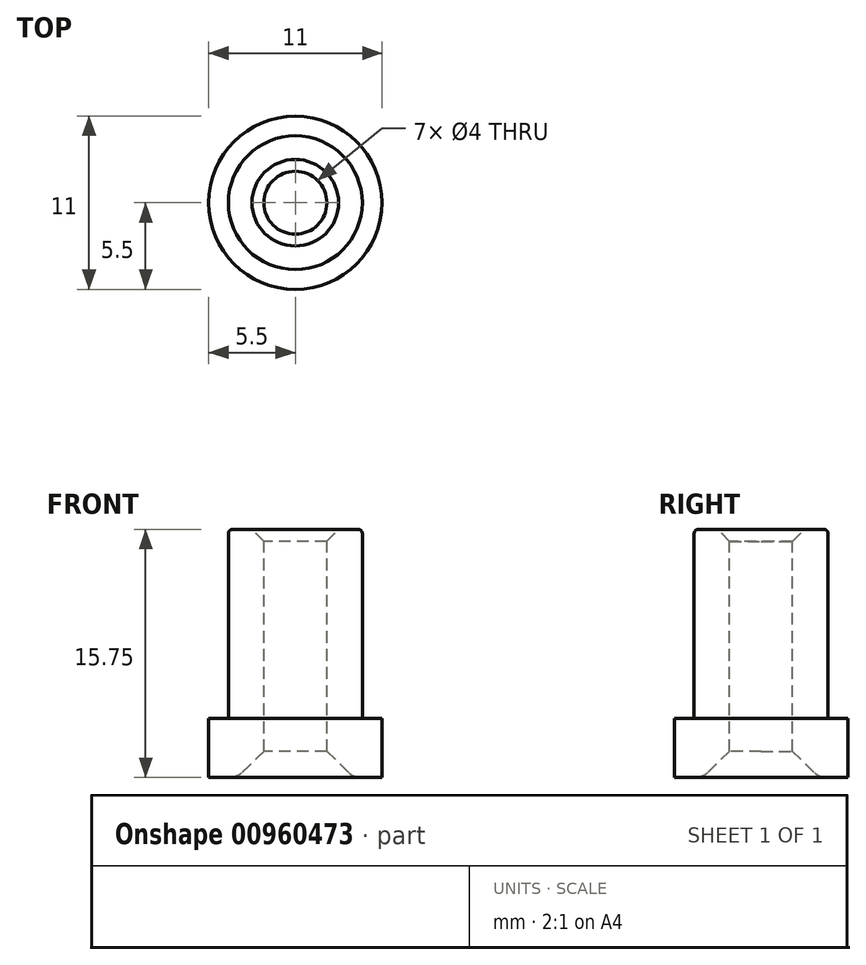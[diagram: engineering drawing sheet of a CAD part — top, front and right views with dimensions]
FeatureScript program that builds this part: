
annotation { "Feature Type Name" : "Feature", "Feature Type Description" : "" }
export const myFeature = defineFeature(function(context is Context, id is Id, definition is map)
    precondition{}
    {
        {
            var Q0;
            Q0=qCreatedBy(makeId("Front.planeOp"),FACE);
            var sketch = newSketch(context, id + "F0", { "sketchPlane" : qUnion([Q0])});
            skLineSegment(sketch, "E0.bottom", {"start": v(-2.75, 9) * mm, "end": v(-8, 9) * mm});
            skLineSegment(sketch, "E0.top", {"start": v(-4.25, -9) * mm, "end": v(-8, -9) * mm});
            skLineSegment(sketch, "E0.right", {"start": v(-9, 8) * mm, "end": v(-9, -8) * mm});
            skPoint(sketch, "E0.middle", {"position": v(0, 0) * mm});
            skLineSegment(sketch, "E1", {"start": v(-2, 8.25) * mm, "end": v(-2, -5.1) * mm});
            skPoint(sketch, "E2.middle", {"position": v(-2, 9) * mm});
            skLineSegment(sketch, "E3", {"start": v(-2.75, 9) * mm, "end": v(-2, 8.25) * mm});
            skPoint(sketch, "E4.orphan", {"position": v(-2.75, 9.75) * mm});
            skPoint(sketch, "E2.left.start.orphan", {"position": v(-2.75, 8.25) * mm});
            skPoint(sketch, "E2.right.end.orphan", {"position": v(-1.25, 9.75) * mm});
            skPoint(sketch, "E2.right.start.orphan", {"position": v(-1.25, 8.25) * mm});
            skLineSegment(sketch, "E5", {"start": v(-4.25, 6.75) * mm, "end": v(-4.25, 9) * mm});
            skLineSegment(sketch, "E6", {"start": v(-5.5, 6) * mm, "end": v(-5.5, -9) * mm});
            skLineSegment(sketch, "E7", {"start": v(-4.25, -3) * mm, "end": v(-4.25, 6.75) * mm});
            skLineSegment(sketch, "E8", {"start": v(-5.5, 6) * mm, "end": v(-4.25, 6) * mm});
            skPoint(sketch, "E9.end.orphan", {"position": v(-3.16, -6.75) * mm});
            skPoint(sketch, "E10.start.orphan", {"position": v(-4.25, -6.75) * mm});
            skLineSegment(sketch, "E11", {"start": v(-4.25, -6.75) * mm, "end": v(-3.7, -6.75) * mm});
            skLineSegment(sketch, "E12", {"start": v(-4.25, -6.75) * mm, "end": v(-5.5, -6.75) * mm});
            skPoint(sketch, "E13.start.orphan", {"position": v(-5.5, -5.5) * mm});
            skPoint(sketch, "E14.end.orphan", {"position": v(-4.88, 6) * mm});
            skPoint(sketch, "E14.start.orphan", {"position": v(-4.88, -5.5) * mm});
            skPoint(sketch, "E15.startSnap0", {"position": v(-5.5, -1.5) * mm});
            skPoint(sketch, "E16.end.orphan", {"position": v(-3.16, -3) * mm});
            skLineSegment(sketch, "E17", {"start": v(-3.7, -6.75) * mm, "end": v(-4.25, -6.75) * mm});
            skLineSegment(sketch, "E18", {"start": v(-3.7, -6.75) * mm, "end": v(-2, -5.1) * mm});
            skPoint(sketch, "E19.center.orphan", {"position": v(0, -9) * mm});
            skPoint(sketch, "E20.visualSharp", {"position": v(-9, 9) * mm});
            skArc(sketch, "E20.filletArc", {"start": v(-8, 9) * mm, "mid": v(-8.7, 8.7) * mm, "end": v(-9, 8) * mm});
            skPoint(sketch, "E21.visualSharp", {"position": v(-9, -9) * mm});
            skArc(sketch, "E21.filletArc", {"start": v(-9, -8) * mm, "mid": v(-8.7, -8.7) * mm, "end": v(-8, -9) * mm});
            skLineSegment(sketch, "E22", {"start": v(0, 9.13) * mm, "end": v(0, -6.61) * mm});
            skPoint(sketch, "E15.start.orphan", {"position": v(-5.5, -3) * mm});
            skLineSegment(sketch, "E23", {"start": v(-5.5, -3) * mm, "end": v(-4.25, -3) * mm});
            skPoint(sketch, "E24.orphan", {"position": v(-4.25, -5.5) * mm});
            skLineSegment(sketch, "E25", {"start": v(-3.7, -6.75) * mm, "end": v(-3.7, -9) * mm});
            skLineSegment(sketch, "E26", {"start": v(-3.7, -9) * mm, "end": v(-4.25, -9) * mm});
            skSolve(sketch);
        }
        {
            var Q0;
            Q0=makeQuery(id+"F0.imprint","IMPRINT",FACE,{"disambiguationData":[TD([[makeQuery(id+"F0.imprint","IMPRINT",EDGE,{"derivedFrom":sQuery(id+"F0.wireOp",EDGE,"E1")}),-1.0]])]});
            var Q1;
            Q1=sQuery(id+"F0.wireOp",EDGE,"E22");
            revolve(context, id + "F1", {"surfaceOperationType" : NewSurfaceOperationType.NEW, "entities" : qUnion([Q0]), "axis" : qUnion([Q1]), "revolveType" : RevolveType.FULL});
        }
        {
            var Q0;
            Q0=makeQuery(id+"F1.opRevolve","SWEPT_EDGE",EDGE,{"disambiguationData":[OSD([sQuery(id+"F0.wireOp",EDGE,"E0.bottom"),sQuery(id+"F0.wireOp",EDGE,"E5")])]});
            fillet(context, id + "F2", {"entities" : qUnion([Q0]), "radius" : .25 * mm, "tangentPropagation" : true, "allowEdgeOverflow" : false});
        }
        {
            var Q0;
            Q0=makeQuery(id+"F1.opRevolve","SWEPT_EDGE",EDGE,{"disambiguationData":[OSD([sQuery(id+"F0.wireOp",EDGE,"E17"),sQuery(id+"F0.wireOp",EDGE,"E18"),sQuery(id+"F0.wireOp",EDGE,"E25")])]});
            fillet(context, id + "F3", {"entities" : qUnion([Q0]), "radius" : 1 * mm, "tangentPropagation" : true, "allowEdgeOverflow" : false});
        }
    });
